# Revit family: Lodges 1000 wide
name_source: partatom
category: Furniture
revit_build: Autodesk Revit 2018 (Build: 20181011_1500(x64)
units: mm (PartAtom-declared; Revit-internal decimal feet)

## family parameters
Always vertical = Yes
Cut with Voids When Loaded = No
OmniClass Number = 23.40.20.00
OmniClass Title = General Furniture and Specialties
Room Calculation Point = No
Shared = No
Work Plane-Based = No

## types (13) — shared parameters
Carcass_Material = Steel, Mild
Category = Lateralfile Lodges
Central Bar Width = 30 mm  [stored 0.0984252 ft]
Compliance Standards Certification = BS EN 14073 2004 Part 2 & 3, BS EN 14074, BS 4875 1998 Part 7 level 4 & Part 8, BS 476 Part 7 1987 Class 2Y
Depth = 470 mm  [stored 1.54199 ft]
Door Height 1 = 377 mm  [stored 1.23688 ft]
Door Height 2 = 377 mm  [stored 1.23688 ft]
Door Height 3 = 377 mm  [stored 1.23688 ft]
Door_Material = Steel, Mild
Drawer_Material = Steel, Mild
Expected Life = 15 Years
Finish = Powder Coated
Lock_Material = Steel AISI 4620
Manufacturer = Bisley
Material = Steel
Mid Bars = 382 mm  [stored 1.25328 ft]
Mid Bars Thickness = 22 mm  [stored 0.0721785 ft]
Mid gaps = 3 mm  [stored 0.00984252 ft]
NamePlate_Material = Plastic
Outer Panels Width = 20 mm  [stored 0.0656168 ft]
Range = Lateralfile Lodges
Routine Maintenance = We recommend you clean your unit with worm water and mild dtergent solution. A damp cloth can be used to remove dust particles.
Uniclass 2015 Code = PR_40_30_78_48
Uniclass2015Title = 78 - Shelves and Storage Units
Uniclass2015Version = V1.1
Warranty = 10 years from date of purchase
Width = 1000 mm  [stored 3.28084 ft]

## per-type parameters (varying)
- L1024SABX2SXP: Bar 0=Yes; Bar 1=No; Bar 2=No; Bar 3=No; Base Panel Height=40 mm  [stored 0.131234 ft]; Bottom Gap=5 mm  [stored 0.0164042 ft]; D Door 1=No; D Door 2=No; D Door 3=No; D Door 4=No; Dimensions=845 x 1000 x 470mm; Door 1=Yes; Door 10=Yes; Door 2=Yes; Door 3=No; Door 4=No; Door 5=No; Door 6=No; Door 7=No; Door 8=No; Door 9=Yes; Drawers=No; Height=845 mm  [stored 2.77231 ft]; Model=L1024ABX2SXP; Model Reference=L1024ABX2SXP; Tollerance=3 mm  [stored 0.00984252 ft]; Top Panel Height=35 mm  [stored 0.114829 ft]; URL=www.bisley.com
- L1036SABX3SXP: Bar 0=Yes; Bar 1=Yes; Bar 2=No; Bar 3=No; Base Panel Height=40 mm  [stored 0.131234 ft]; Bottom Gap=3 mm  [stored 0.00984252 ft]; D Door 1=No; D Door 2=No; D Door 3=No; D Door 4=No; Dimensions=1225 x 1000 x 470mm; Door 1=Yes; Door 10=Yes; Door 2=Yes; Door 3=Yes; Door 4=Yes; Door 5=No; Door 6=No; Door 7=No; Door 8=No; Door 9=Yes; Drawers=No; Height=1225 mm  [stored 4.01903 ft]; Model=L1036SABX3SXP; Model Reference=L1036SABX3SXP; Tollerance=2 mm  [stored 0.00656168 ft]; Top Panel Height=40 mm  [stored 0.131234 ft]; URL=www.bisley.com
- L1048SABX4SXP: Bar 0=Yes; Bar 1=Yes; Bar 2=Yes; Bar 3=No; Base Panel Height=45 mm  [stored 0.147638 ft]; Bottom Gap=2 mm  [stored 0.00656168 ft]; D Door 1=No; D Door 2=No; D Door 3=No; D Door 4=No; Dimensions=1605 x 1000 x 470mm; Door 1=Yes; Door 10=Yes; Door 2=Yes; Door 3=Yes; Door 4=Yes; Door 5=Yes; Door 6=Yes; Door 7=No; Door 8=No; Door 9=Yes; Drawers=No; Height=1605 mm  [stored 5.26575 ft]; Model=L1048SABX4SXP; Model Reference=L1048SABX4SXP; Tollerance=2 mm  [stored 0.00656168 ft]; Top Panel Height=40 mm  [stored 0.131234 ft]; URL=www.bisley.com
- L1061SABX5SXP: Bar 0=Yes; Bar 1=Yes; Bar 2=Yes; Bar 3=Yes; Base Panel Height=40 mm  [stored 0.131234 ft]; Bottom Gap=3 mm  [stored 0.00984252 ft]; D Door 1=No; D Door 2=No; D Door 3=No; D Door 4=No; Dimensions=1985 x 1000 x 470; Door 1=Yes; Door 10=Yes; Door 2=Yes; Door 3=Yes; Door 4=Yes; Door 5=Yes; Door 6=Yes; Door 7=Yes; Door 8=Yes; Door 9=Yes; Drawers=No; Height=1985 mm  [stored 6.51247 ft]; Model=L1061SABX5SXP; Model Reference=L1061SABX5SXP; Tollerance=2 mm  [stored 0.00656168 ft]; Top Panel Height=40 mm  [stored 0.131234 ft]; URL=www.bisley.com
- L1024SABXDXP: Bar 0=No; Bar 1=No; Bar 2=No; Bar 3=No; Base Panel Height=40 mm  [stored 0.131234 ft]; Bottom Gap=5 mm  [stored 0.0164042 ft]; D Door 1=Yes; D Door 2=Yes; D Door 3=No; D Door 4=No; Dimensions=845 x 1000 x 470mm; Door 1=No; Door 10=No; Door 2=No; Door 3=No; Door 4=No; Door 5=No; Door 6=No; Door 7=No; Door 8=No; Door 9=No; Drawers=No; Height=845 mm  [stored 2.77231 ft]; Model=L1024SABXDXP; Model Reference=L1024SABXDXP; Tollerance=3 mm  [stored 0.00984252 ft]; Top Panel Height=40 mm  [stored 0.131234 ft]; URL=www.bisley.com
- L1036SABXSDXP: Bar 0=No; Bar 1=Yes; Bar 2=No; Bar 3=No; Base Panel Height=40 mm  [stored 0.131234 ft]; Bottom Gap=3 mm  [stored 0.00984252 ft]; D Door 1=Yes; D Door 2=Yes; D Door 3=No; D Door 4=No; Dimensions=1225 x 1000 x 470mm; Door 1=No; Door 10=Yes; Door 2=No; Door 3=No; Door 4=No; Door 5=No; Door 6=No; Door 7=No; Door 8=No; Door 9=Yes; Drawers=No; Height=1225 mm  [stored 4.01903 ft]; Model=L1036SABXSDXP; Model Reference=L1036SABXSDXP; Tollerance=2 mm  [stored 0.00656168 ft]; Top Panel Height=40 mm  [stored 0.131234 ft]; URL=WWW.bisley.com
- L1048SABX2SDXP: Bar 0=No; Bar 1=Yes; Bar 2=Yes; Bar 3=No; Base Panel Height=45 mm  [stored 0.147638 ft]; Bottom Gap=2 mm  [stored 0.00656168 ft]; D Door 1=Yes; D Door 2=Yes; D Door 3=No; D Door 4=No; Dimensions=1605 x 1000 x 470mm; Door 1=No; Door 10=Yes; Door 2=No; Door 3=No; Door 4=No; Door 5=Yes; Door 6=Yes; Door 7=No; Door 8=No; Door 9=Yes; Drawers=No; Height=1605 mm  [stored 5.26575 ft]; Model=L1048SABX2SDXP; Model Reference=L1048SABX2SDXP; Tollerance=2 mm  [stored 0.00656168 ft]; Top Panel Height=40 mm  [stored 0.131234 ft]; URL=www.bisley.com
- L1061SABX3SDXP: Bar 0=No; Bar 1=Yes; Bar 2=Yes; Bar 3=Yes; Base Panel Height=40 mm  [stored 0.131234 ft]; Bottom Gap=3 mm  [stored 0.00984252 ft]; D Door 1=Yes; D Door 2=Yes; D Door 3=No; D Door 4=No; Dimensions=1985 x 1000 x 470mm; Door 1=No; Door 10=Yes; Door 2=No; Door 3=No; Door 4=No; Door 5=Yes; Door 6=Yes; Door 7=Yes; Door 8=Yes; Door 9=Yes; Drawers=No; Height=1985 mm  [stored 6.51247 ft]; Model=L1061SABX3SDXP; Model Reference=L1061SABX3SDXP; Tollerance=2 mm  [stored 0.00656168 ft]; Top Panel Height=40 mm  [stored 0.131234 ft]; URL=www.bisley.com
- L1061SABXD3SXP: Bar 0=Yes; Bar 1=Yes; Bar 2=Yes; Bar 3=No; Base Panel Height=40 mm  [stored 0.131234 ft]; Bottom Gap=3 mm  [stored 0.00984252 ft]; D Door 1=No; D Door 2=No; D Door 3=Yes; D Door 4=Yes; Dimensions=1985 x 1000 x 470; Door 1=Yes; Door 10=No; Door 2=Yes; Door 3=Yes; Door 4=Yes; Door 5=Yes; Door 6=Yes; Door 7=No; Door 8=No; Door 9=No; Drawers=No; Height=1985 mm  [stored 6.51247 ft]; Model=L1061SABXD3SXP; Model Reference=L1061SABXD3SXP; Tollerance=2 mm  [stored 0.00656168 ft]; Top Panel Height=40 mm  [stored 0.131234 ft]; URL=www.bisley.com
- L1061SABX4SPXP: Bar 0=Yes; Bar 1=Yes; Bar 2=Yes; Bar 3=Yes; Base Panel Height=40 mm  [stored 0.131234 ft]; Bottom Gap=3 mm  [stored 0.00984252 ft]; D Door 1=No; D Door 2=No; D Door 3=No; D Door 4=No; Dimensions=1985 x 1000 x 470mm; Door 1=No; Door 10=Yes; Door 2=No; Door 3=Yes; Door 4=Yes; Door 5=Yes; Door 6=Yes; Door 7=Yes; Door 8=Yes; Door 9=Yes; Drawers=Yes; Height=1985 mm  [stored 6.51247 ft]; Model=L1061SABX4SPXP; Model Reference=L1061SABX4SPXP; Tollerance=2 mm  [stored 0.00656168 ft]; Top Panel Height=40 mm  [stored 0.131234 ft]; URL=www.bisley.com
- L1048SABX3PXP: Bar 0=Yes; Bar 1=Yes; Bar 2=Yes; Bar 3=No; Base Panel Height=45 mm  [stored 0.147638 ft]; Bottom Gap=2 mm  [stored 0.00656168 ft]; D Door 1=No; D Door 2=No; D Door 3=No; D Door 4=No; Dimensions=1605 x 1000 x 470mm; Door 1=No; Door 10=Yes; Door 2=No; Door 3=Yes; Door 4=Yes; Door 5=Yes; Door 6=Yes; Door 7=No; Door 8=No; Door 9=Yes; Drawers=Yes; Height=1605 mm  [stored 5.26575 ft]; Model=L1048SABX3PXP; Model Reference=L1048SABX3PXP; Tollerance=2 mm  [stored 0.00656168 ft]; Top Panel Height=40 mm  [stored 0.131234 ft]; URL=www.bisley.com
- L1036SABX2SPXP: Bar 0=Yes; Bar 1=Yes; Bar 2=No; Bar 3=No; Base Panel Height=40 mm  [stored 0.131234 ft]; Bottom Gap=3 mm  [stored 0.00984252 ft]; D Door 1=No; D Door 2=No; D Door 3=No; D Door 4=No; Dimensions=1225 x 1000 x 470mm; Door 1=No; Door 10=Yes; Door 2=No; Door 3=Yes; Door 4=Yes; Door 5=No; Door 6=No; Door 7=No; Door 8=No; Door 9=Yes; Drawers=Yes; Height=1225 mm  [stored 4.01903 ft]; Model=L1036SABX2SPXP; Model Reference=L1036SABX2SPXP; Tollerance=2 mm  [stored 0.00656168 ft]; Top Panel Height=40 mm  [stored 0.131234 ft]; URL=www.bisley.com
- L1024SABXSPXP: Bar 0=Yes; Bar 1=No; Bar 2=No; Bar 3=No; Base Panel Height=40 mm  [stored 0.131234 ft]; Bottom Gap=5 mm  [stored 0.0164042 ft]; D Door 1=No; D Door 2=No; D Door 3=No; D Door 4=No; Dimensions=845 x 1000 x 470mm; Door 1=No; Door 10=Yes; Door 2=No; Door 3=No; Door 4=No; Door 5=No; Door 6=No; Door 7=No; Door 8=No; Door 9=Yes; Drawers=Yes; Height=845 mm  [stored 2.77231 ft]; Model=L1024SABXSPXP; Model Reference=L1024SABXSPXP; Tollerance=3 mm  [stored 0.00984252 ft]; Top Panel Height=40 mm  [stored 0.131234 ft]; URL=www.bisley.com

note: [stored X ft] marks values corroborated as IEEE doubles in the binary element streams (Revit-internal decimal feet)

## geometry (parser evidence)
native form markers: Sweep x39
no freeform markers — native parametric forms only
